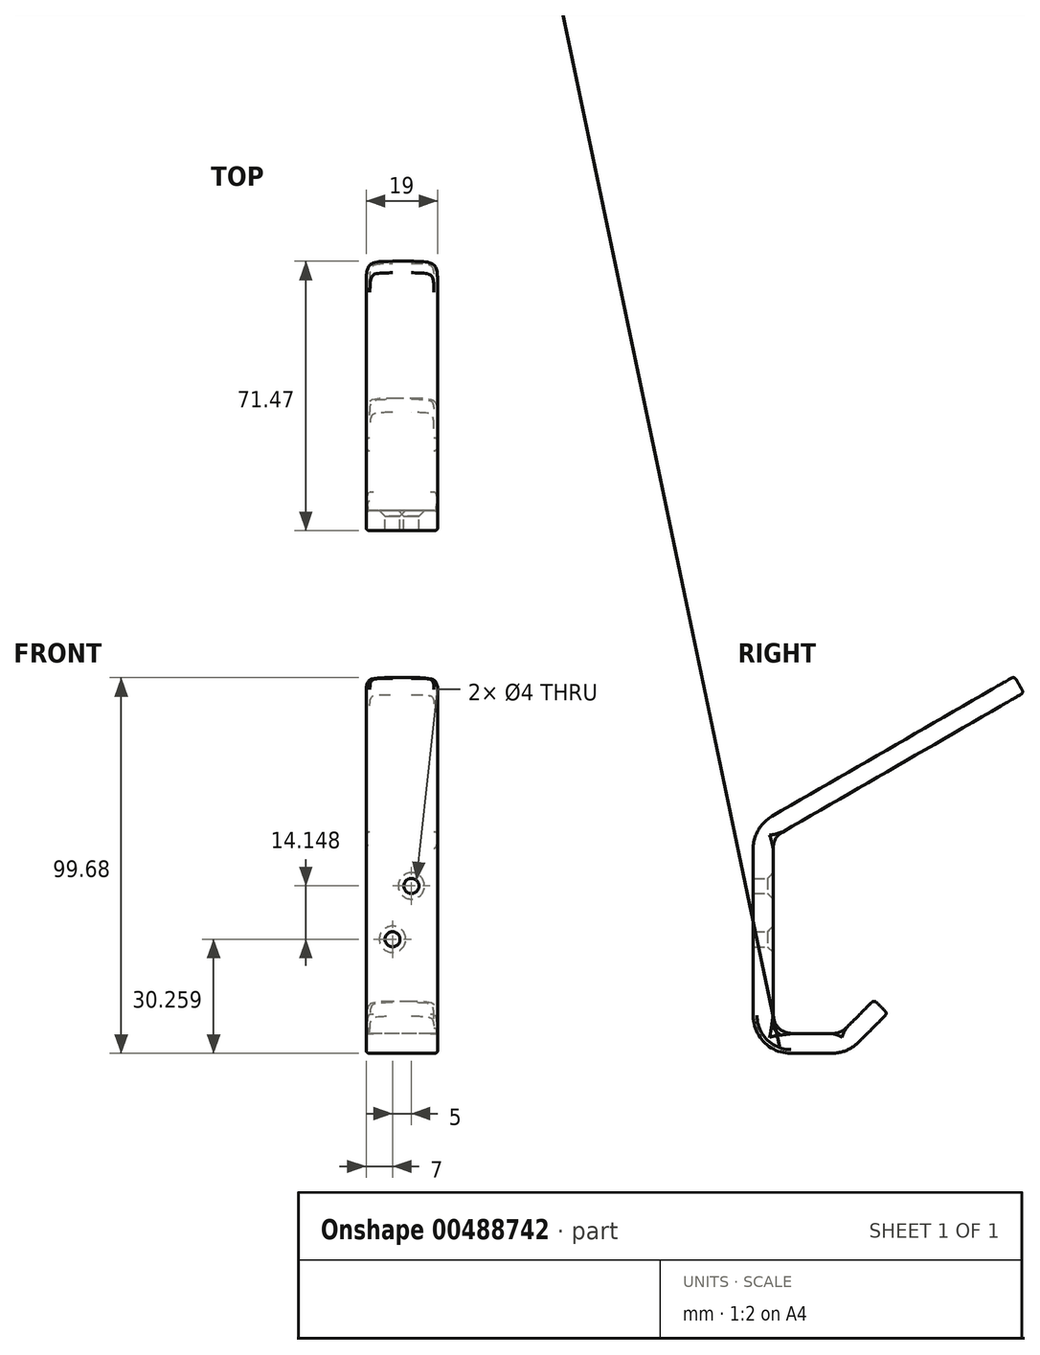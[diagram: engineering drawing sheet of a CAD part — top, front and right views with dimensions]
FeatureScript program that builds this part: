
annotation { "Feature Type Name" : "Feature", "Feature Type Description" : "" }
export const myFeature = defineFeature(function(context is Context, id is Id, definition is map)
    precondition{}
    {
        {
            var Q0;
            Q0=qCreatedBy(makeId("Right.planeOp"),FACE);
            var sketch = newSketch(context, id + "F0", { "sketchPlane" : qUnion([Q0])});
            skLineSegment(sketch, "E0", {"start": v(-25, 0) * mm, "end": v(-25, 60) * mm});
            skLineSegment(sketch, "E1", {"start": v(-19.69, 5.26) * mm, "end": v(-19.69, 57.3) * mm});
            skLineSegment(sketch, "E2", {"start": v(44.28, 100) * mm, "end": v(46.78, 95.67) * mm});
            skLineSegment(sketch, "E3", {"start": v(46.78, 95.67) * mm, "end": v(-19.69, 57.3) * mm});
            skLineSegment(sketch, "E4", {"start": v(44.28, 100) * mm, "end": v(-25, 60) * mm});
            skLineSegment(sketch, "E5", {"start": v(-25, 0) * mm, "end": v(0, 0) * mm});
            skLineSegment(sketch, "E6", {"start": v(0, 0) * mm, "end": v(10.6, 10.6) * mm});
            skLineSegment(sketch, "E7", {"start": v(10.6, 10.6) * mm, "end": v(7.07, 14.14) * mm});
            skLineSegment(sketch, "E8", {"start": v(7.07, 14.14) * mm, "end": v(-1.81, 5.26) * mm});
            skLineSegment(sketch, "E9", {"start": v(-19.69, 5.26) * mm, "end": v(-1.81, 5.26) * mm});
            skSolve(sketch);
        }
        {
            var Q0;
            Q0 = qSketchRegion(id + "F0", true);
            extrude(context, id + "F1", {"entities" : qUnion([Q0]), "depth" : 19 * mm, "offsetDistance" : 25 * mm});
        }
        {
            var Q0;
            Q0=makeQuery(id+"F1.opExtrude","CAP_EDGE",EDGE,{"disambiguationData":[OSD([sQuery(id+"F0.wireOp",EDGE,"E7")])],"isStart":false});
            var Q1;
            Q1=makeQuery(id+"F1.opExtrude","CAP_EDGE",EDGE,{"disambiguationData":[OSD([sQuery(id+"F0.wireOp",EDGE,"E7")])],"isStart":true});
            fillet(context, id + "F2", {"entities" : qUnion([Q0, Q1]), "radius" : 7 * mm, "tangentPropagation" : true, "rho" : 0.7, "crossSection" : FilletCrossSection.CONIC, "allowEdgeOverflow" : false});
        }
        {
            var Q0;
            Q0=makeQuery(id+"F1.opExtrude","CAP_EDGE",EDGE,{"disambiguationData":[OSD([sQuery(id+"F0.wireOp",EDGE,"E9")])],"isStart":true});
            fillet(context, id + "F3", {"entities" : qUnion([Q0]), "radius" : 1 * mm, "tangentPropagation" : true, "rho" : 0.5, "crossSection" : FilletCrossSection.CONIC, "allowEdgeOverflow" : false});
        }
        {
            var Q0;
            Q0=makeQuery(id+"F1.opExtrude","CAP_EDGE",EDGE,{"disambiguationData":[OSD([sQuery(id+"F0.wireOp",EDGE,"E8")])],"isStart":true});
            fillet(context, id + "F4", {"entities" : qUnion([Q0]), "radius" : 1 * mm, "tangentPropagation" : true, "rho" : 0.5, "crossSection" : FilletCrossSection.CONIC, "allowEdgeOverflow" : false});
        }
        {
            var Q0;
            Q0=makeQuery(id+"F1.opExtrude","CAP_EDGE",EDGE,{"disambiguationData":[OSD([sQuery(id+"F0.wireOp",EDGE,"E9")])],"isStart":false});
            fillet(context, id + "F5", {"entities" : qUnion([Q0]), "radius" : 1 * mm, "tangentPropagation" : true, "rho" : 0.5, "crossSection" : FilletCrossSection.CONIC, "allowEdgeOverflow" : false});
        }
        {
            var Q0;
            Q0=makeQuery(id+"F1.opExtrude","CAP_EDGE",EDGE,{"disambiguationData":[OSD([sQuery(id+"F0.wireOp",EDGE,"E1")])],"isStart":false});
            var Q1;
            Q1=makeQuery(id+"F1.opExtrude","CAP_EDGE",EDGE,{"disambiguationData":[OSD([sQuery(id+"F0.wireOp",EDGE,"E1")])],"isStart":true});
            fillet(context, id + "F6", {"entities" : qUnion([Q0, Q1]), "radius" : 1 * mm, "tangentPropagation" : true, "rho" : 0.5, "crossSection" : FilletCrossSection.CONIC, "allowEdgeOverflow" : false});
        }
        {
            var Q0;
            Q0=makeQuery(id+"F1.opExtrude","CAP_EDGE",EDGE,{"disambiguationData":[OSD([sQuery(id+"F0.wireOp",EDGE,"E2")])],"isStart":false});
            var Q1;
            Q1=makeQuery(id+"F1.opExtrude","CAP_EDGE",EDGE,{"disambiguationData":[OSD([sQuery(id+"F0.wireOp",EDGE,"E2")])],"isStart":true});
            fillet(context, id + "F7", {"entities" : qUnion([Q0, Q1]), "radius" : 7 * mm, "tangentPropagation" : true, "rho" : 0.7, "crossSection" : FilletCrossSection.CONIC, "allowEdgeOverflow" : false});
        }
        {
            var Q0;
            Q0=makeQuery(id+"F1.opExtrude","CAP_EDGE",EDGE,{"disambiguationData":[OSD([sQuery(id+"F0.wireOp",EDGE,"E3")])],"isStart":false});
            var Q1;
            Q1=makeQuery(id+"F7.opFillet","BLEND_EDGE",EDGE,{"blendedFrom":[makeQuery(id+"F1.opExtrude","CAP_EDGE",EDGE,{"disambiguationData":[OSD([sQuery(id+"F0.wireOp",EDGE,"E2")])],"isStart":false}),makeQuery(id+"F1.opExtrude","SWEPT_FACE",FACE,{"disambiguationData":[OSD([sQuery(id+"F0.wireOp",EDGE,"E3")])]})],"blendedInto":[makeQuery(id+"F1.opExtrude","SWEPT_FACE",FACE,{"disambiguationData":[OSD([sQuery(id+"F0.wireOp",EDGE,"E3")])]})]});
            var Q2;
            Q2=makeQuery(id+"F1.opExtrude","SWEPT_EDGE",EDGE,{"disambiguationData":[OSD([sQuery(id+"F0.wireOp",EDGE,"E2"),sQuery(id+"F0.wireOp",EDGE,"E3")])]});
            var Q3;
            Q3=makeQuery(id+"F7.opFillet","BLEND_EDGE",EDGE,{"blendedFrom":[makeQuery(id+"F1.opExtrude","CAP_EDGE",EDGE,{"disambiguationData":[OSD([sQuery(id+"F0.wireOp",EDGE,"E2")])],"isStart":true}),makeQuery(id+"F1.opExtrude","SWEPT_FACE",FACE,{"disambiguationData":[OSD([sQuery(id+"F0.wireOp",EDGE,"E3")])]})],"blendedInto":[makeQuery(id+"F1.opExtrude","SWEPT_FACE",FACE,{"disambiguationData":[OSD([sQuery(id+"F0.wireOp",EDGE,"E3")])]})]});
            var Q4;
            Q4=makeQuery(id+"F1.opExtrude","CAP_EDGE",EDGE,{"disambiguationData":[OSD([sQuery(id+"F0.wireOp",EDGE,"E3")])],"isStart":true});
            fillet(context, id + "F8", {"entities" : qUnion([Q0, Q1, Q2, Q3, Q4]), "radius" : 1 * mm, "tangentPropagation" : true, "rho" : 0.5, "crossSection" : FilletCrossSection.CONIC, "allowEdgeOverflow" : false});
        }
        {
            var Q0;
            Q0=makeQuery(id+"F1.opExtrude","SWEPT_EDGE",EDGE,{"disambiguationData":[OSD([sQuery(id+"F0.wireOp",EDGE,"E1"),sQuery(id+"F0.wireOp",EDGE,"E3")])]});
            fillet(context, id + "F9", {"entities" : qUnion([Q0]), "radius" : 5 * mm, "tangentPropagation" : true, "rho" : 0.5, "crossSection" : FilletCrossSection.CONIC, "allowEdgeOverflow" : false});
        }
        {
            var Q0;
            Q0=makeQuery(id+"F1.opExtrude","SWEPT_EDGE",EDGE,{"disambiguationData":[OSD([sQuery(id+"F0.wireOp",EDGE,"E1"),sQuery(id+"F0.wireOp",EDGE,"E9")])]});
            fillet(context, id + "F10", {"entities" : qUnion([Q0]), "radius" : 5 * mm, "tangentPropagation" : true, "allowEdgeOverflow" : false});
        }
        {
            var Q0;
            Q0=makeQuery(id+"F1.opExtrude","SWEPT_EDGE",EDGE,{"disambiguationData":[OSD([sQuery(id+"F0.wireOp",EDGE,"E0"),sQuery(id+"F0.wireOp",EDGE,"E4")])]});
            fillet(context, id + "F11", {"entities" : qUnion([Q0]), "radius" : 10 * mm, "tangentPropagation" : true, "allowEdgeOverflow" : false});
        }
        {
            var Q0;
            Q0=makeQuery(id+"F1.opExtrude","SWEPT_EDGE",EDGE,{"disambiguationData":[OSD([sQuery(id+"F0.wireOp",EDGE,"E0"),sQuery(id+"F0.wireOp",EDGE,"E5")])]});
            fillet(context, id + "F12", {"entities" : qUnion([Q0]), "radius" : 10 * mm, "tangentPropagation" : true, "allowEdgeOverflow" : false});
        }
        {
            var Q0;
            Q0=makeQuery(id+"F1.opExtrude","SWEPT_EDGE",EDGE,{"disambiguationData":[OSD([sQuery(id+"F0.wireOp",EDGE,"E8"),sQuery(id+"F0.wireOp",EDGE,"E9")])]});
            fillet(context, id + "F13", {"entities" : qUnion([Q0]), "radius" : 5 * mm, "tangentPropagation" : true, "allowEdgeOverflow" : false});
        }
        {
            var Q0;
            Q0=makeQuery(id+"F1.opExtrude","SWEPT_EDGE",EDGE,{"disambiguationData":[OSD([sQuery(id+"F0.wireOp",EDGE,"E5"),sQuery(id+"F0.wireOp",EDGE,"E6")])]});
            fillet(context, id + "F14", {"entities" : qUnion([Q0]), "radius" : 10 * mm, "tangentPropagation" : true, "allowEdgeOverflow" : false});
        }
        {
            var Q0;
            Q0=makeQuery(id+"F1.opExtrude","CAP_EDGE",EDGE,{"disambiguationData":[OSD([sQuery(id+"F0.wireOp",EDGE,"E6")])],"isStart":false});
            fillet(context, id + "F15", {"entities" : qUnion([Q0]), "radius" : 1 * mm, "tangentPropagation" : true, "rho" : 0.5, "crossSection" : FilletCrossSection.CONIC, "allowEdgeOverflow" : false});
        }
        {
            var Q0;
            Q0=makeQuery(id+"F1.opExtrude","SWEPT_FACE",FACE,{"disambiguationData":[OSD([sQuery(id+"F0.wireOp",EDGE,"E1")])]});
            var sketch = newSketch(context, id + "F16", { "sketchPlane" : qUnion([Q0])});
            skLineSegment(sketch, "E10", {"start": v(-12, 54.4) * mm, "end": v(-12, 44.4) * mm});
            skLineSegment(sketch, "E11", {"start": v(-12, 44.4) * mm, "end": v(-18, 44.4) * mm});
            skLineSegment(sketch, "E12", {"start": v(-1, 30.26) * mm, "end": v(-7, 30.26) * mm});
            skLineSegment(sketch, "E13", {"start": v(-7, 30.26) * mm, "end": v(-7, 10.26) * mm});
            skPoint(sketch, "E14", {"position": v(-7, 30.26) * mm});
            skSolve(sketch);
        }
        {
            var Q0;
            Q0=sQuery(id+"F16.wireOp",VERTEX,"E11.start");
            var Q1;
            Q1=makeQuery(id+"F1.opExtrude","SWEPT_BODY",BODY,{"disambiguationData":[OSD([sQuery(id+"F0.wireOp",EDGE,"E0"),sQuery(id+"F0.wireOp",EDGE,"E1"),sQuery(id+"F0.wireOp",EDGE,"E2"),sQuery(id+"F0.wireOp",EDGE,"E3"),sQuery(id+"F0.wireOp",EDGE,"E4"),sQuery(id+"F0.wireOp",EDGE,"E5"),sQuery(id+"F0.wireOp",EDGE,"E6"),sQuery(id+"F0.wireOp",EDGE,"E7"),sQuery(id+"F0.wireOp",EDGE,"E8"),sQuery(id+"F0.wireOp",EDGE,"E9")])]});
            hole(context, id + "F17", {"style" : HoleStyle.C_SINK, "endStyle" : HoleEndStyle.THROUGH, "holeDiameter" : 4 * mm, "cSinkDiameter" : 7 * mm, "cSinkAngle" : 90 * degree, "isTappedThrough" : true, "tappedDepth" : 12 * mm, "tapClearance" : 3, "locations" : qUnion([Q0]), "scope" : qUnion([Q1])});
        }
        {
            var Q0;
            Q0=sQuery(id+"F16.wireOp",VERTEX,"E14");
            var Q1;
            Q1=makeQuery(id+"F1.opExtrude","SWEPT_BODY",BODY,{"disambiguationData":[OSD([sQuery(id+"F0.wireOp",EDGE,"E0"),sQuery(id+"F0.wireOp",EDGE,"E1"),sQuery(id+"F0.wireOp",EDGE,"E2"),sQuery(id+"F0.wireOp",EDGE,"E3"),sQuery(id+"F0.wireOp",EDGE,"E4"),sQuery(id+"F0.wireOp",EDGE,"E5"),sQuery(id+"F0.wireOp",EDGE,"E6"),sQuery(id+"F0.wireOp",EDGE,"E7"),sQuery(id+"F0.wireOp",EDGE,"E8"),sQuery(id+"F0.wireOp",EDGE,"E9")])]});
            hole(context, id + "F18", {"style" : HoleStyle.C_SINK, "endStyle" : HoleEndStyle.THROUGH, "holeDiameter" : 4 * mm, "cSinkDiameter" : 7 * mm, "cSinkAngle" : 90 * degree, "isTappedThrough" : true, "tappedDepth" : 12 * mm, "tapClearance" : 3, "locations" : qUnion([Q0]), "scope" : qUnion([Q1])});
        }
    });
